# Revit family: PARLÉ TTM-X - Network Box_rev0
name_source: partatom
category: Communication Devices
units: mm (PartAtom-declared; Revit-internal decimal feet)

## family parameters
Cut with Voids When Loaded = No
Host = Face
Maintain Annotation Orientation = No
Part Type = Normal
Room Calculation Point = Yes
Round Connector Dimension = Use Diameter
Shared = Yes

## types (1)
- PARLÉ™ TTM-X Network Box
    Case Finish = Black Finish
    Connector = Three RJ-45: one between TTM-X network box and switch, one between the network box and microphone, the other between TCM-X network box and TCM-XEX
    Default Elevation = 0' - 0"
    Depth = 0' - 4 29/32"
    Description = AVB low-profle ceiling microphone (Network Box only. Refer to TTM-X/TTM-XEX mic for additional data and cost)
    Height = 0' - 0 29/32"
    Manufacturer = Biamp Systems
    Manufacturer URL = https://www.biamp.com
    Max Distance Between Devices = 33 feet (10 meters) between TTM-XEX and DSP host device
    Model = Parlé TTM-X  Network Box
    POE Power = 15.4
    Power = PoE (IEEE 802.3at Class 3, 15.4W)
    Regulatory Compliance = FCC Part 15B (USA) CE marked (Europe) UL and C-UL listed (USA and Canada) RoHS Directive (Europe) Evaluated to the requirements of UL 2043 and is suitable for use in air handling spaces
    Weight Product = 0.7
    Width = 0' - 4 3/16"

## geometry (parser evidence)
native form markers: Sweep x2
no freeform markers — native parametric forms only
